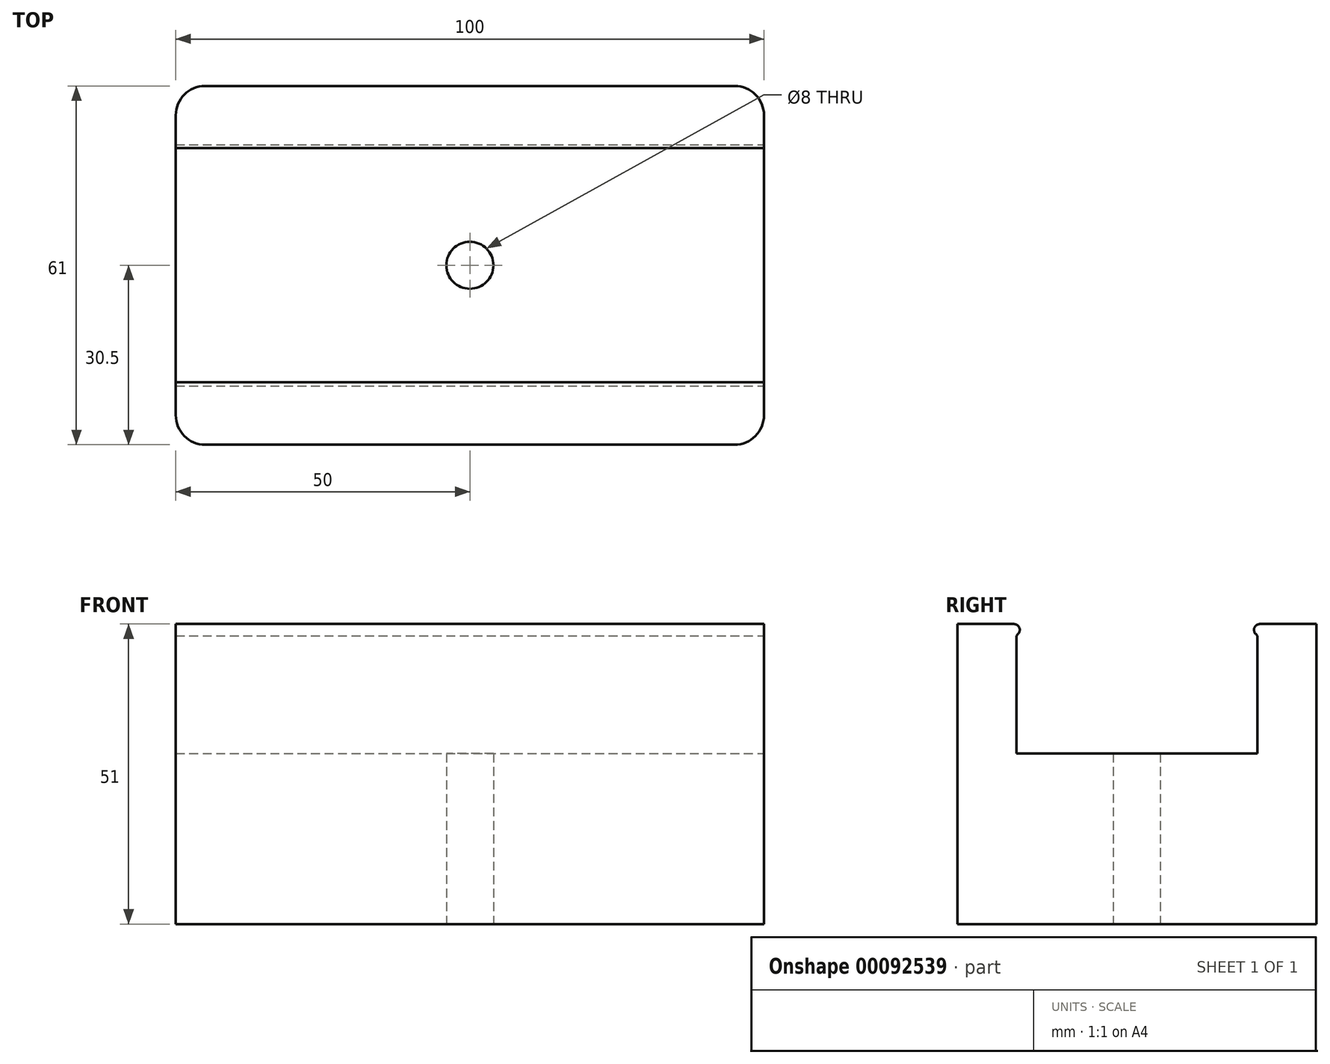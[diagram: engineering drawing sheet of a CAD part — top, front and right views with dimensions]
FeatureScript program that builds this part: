
annotation { "Feature Type Name" : "Feature", "Feature Type Description" : "" }
export const myFeature = defineFeature(function(context is Context, id is Id, definition is map)
    precondition{}
    {
        {
            var Q0;
            Q0=qCreatedBy(makeId("Top.planeOp"),FACE);
            var sketch = newSketch(context, id + "F0", { "sketchPlane" : qUnion([Q0])});
            skLineSegment(sketch, "E0.bottom", {"start": v(0, 0) * mm, "end": v(100, 0) * mm});
            skLineSegment(sketch, "E0.top", {"start": v(0, -61) * mm, "end": v(100, -61) * mm});
            skLineSegment(sketch, "E0.left", {"start": v(0, 0) * mm, "end": v(0, -61) * mm});
            skLineSegment(sketch, "E0.right", {"start": v(100, 0) * mm, "end": v(100, -61) * mm});
            skLineSegment(sketch, "E1", {"start": v(0, -30.5) * mm, "end": v(100, -30.5) * mm});
            skLineSegment(sketch, "E2", {"start": v(0, -51) * mm, "end": v(100, -51) * mm});
            skLineSegment(sketch, "E3", {"start": v(0, -10) * mm, "end": v(100, -10) * mm});
            skLineSegment(sketch, "E4", {"start": v(100, -10) * mm, "end": v(100, -30.5) * mm});
            skLineSegment(sketch, "E5", {"start": v(100, -51) * mm, "end": v(100, -30.5) * mm});
            skCircle(sketch, "E6", {"center": v(50, -30.5) * mm, "radius": 4 * mm});
            skCircle(sketch, "E7", {"center": v(50, -30.5) * mm, "radius": 1 * mm});
            skSolve(sketch);
        }
        {
            var Q0;
            {var subQ0=sQuery(id+"F0.wireOp",EDGE,"E0.bottom");Q0=makeQuery(id+"F0.imprint","IMPRINT",FACE,{"disambiguationData":[TD([[makeQuery(id+"F0.imprint","IMPRINT",EDGE,{"derivedFrom":subQ0}),-1.0]])]});}
            var Q1;
            {var subQ0=sQuery(id+"F0.wireOp",EDGE,"E0.top");Q1=makeQuery(id+"F0.imprint","IMPRINT",FACE,{"disambiguationData":[TD([[makeQuery(id+"F0.imprint","IMPRINT",EDGE,{"derivedFrom":subQ0}),1.0]])]});}
            extrude(context, id + "F1", {"entities" : qUnion([Q0, Q1]), "depth" : 51 * mm});
        }
        {
            var Q0;
            {var subQ0=sQuery(id+"F0.wireOp",EDGE,"E0.bottom");Q0=makeQuery(id+"F0.imprint","IMPRINT",FACE,{"disambiguationData":[TD([[makeQuery(id+"F0.imprint","IMPRINT",EDGE,{"derivedFrom":subQ0}),-1.0]])]});}
            var Q1;
            {var subQ0=sQuery(id+"F0.wireOp",EDGE,"E0.top");Q1=makeQuery(id+"F0.imprint","IMPRINT",FACE,{"disambiguationData":[TD([[makeQuery(id+"F0.imprint","IMPRINT",EDGE,{"derivedFrom":subQ0}),1.0]])]});}
            var Q2;
            {var subQ8=sQuery(id+"F0.wireOp",EDGE,"E3");Q2=makeQuery(id+"F0.imprint","IMPRINT",FACE,{"disambiguationData":[TD([[makeQuery(id+"F0.imprint","IMPRINT",EDGE,{"derivedFrom":subQ8}),-1.0]])]});}
            var Q3;
            {var subQ8=sQuery(id+"F0.wireOp",EDGE,"E2");Q3=makeQuery(id+"F0.imprint","IMPRINT",FACE,{"disambiguationData":[TD([[makeQuery(id+"F0.imprint","IMPRINT",EDGE,{"derivedFrom":subQ8}),1.0]])]});}
            extrude(context, id + "F2", {"entities" : qUnion([Q0, Q1, Q2, Q3]), "depth" : 26 * mm});
        }
        {
            var Q0;
            {var subQ0=sQuery(id+"F0.wireOp",EDGE,"E6");var subQ1=sQuery(id+"F0.wireOp",EDGE,"E1");var subQ2=makeQuery(id+"F0.imprint","INTERSECT",VERTEX,{"disambiguationData":[OD(0.0)],"derivedFrom":[subQ1,subQ0]});Q0=makeQuery(id+"F0.imprint","IMPRINT",FACE,{"disambiguationData":[TD([[makeQuery(id+"F0.imprint","IMPRINT",EDGE,{"disambiguationData":[TD([[subQ2,1.0]])],"derivedFrom":subQ1}),1.0]])]});}
            var Q1;
            {var subQ0=sQuery(id+"F0.wireOp",EDGE,"E6");var subQ1=sQuery(id+"F0.wireOp",EDGE,"E1");var subQ2=makeQuery(id+"F0.imprint","INTERSECT",VERTEX,{"disambiguationData":[OD(0.0)],"derivedFrom":[subQ1,subQ0]});Q1=makeQuery(id+"F0.imprint","IMPRINT",FACE,{"disambiguationData":[TD([[makeQuery(id+"F0.imprint","IMPRINT",EDGE,{"disambiguationData":[TD([[subQ2,1.0]])],"derivedFrom":subQ1}),-1.0]])]});}
            extrude(context, id + "F3", {"entities" : qUnion([Q0, Q1]), "operationType" : NewBodyOperationType.ADD, "depth" : 29 * mm});
        }
        {
            var Q0;
            Q0=makeQuery(id+"F1.opExtrude","SWEPT_EDGE",EDGE,{"disambiguationData":[OSD([sQuery(id+"F0.wireOp",EDGE,"E0.bottom"),sQuery(id+"F0.wireOp",EDGE,"E0.right")])]});
            var Q1;
            Q1=makeQuery(id+"F1.opExtrude","SWEPT_EDGE",EDGE,{"disambiguationData":[OSD([sQuery(id+"F0.wireOp",EDGE,"E0.bottom"),sQuery(id+"F0.wireOp",EDGE,"E0.left")])]});
            var Q2;
            Q2=makeQuery(id+"F1.opExtrude","SWEPT_EDGE",EDGE,{"disambiguationData":[OSD([sQuery(id+"F0.wireOp",EDGE,"E0.top"),sQuery(id+"F0.wireOp",EDGE,"E0.right")])]});
            var Q3;
            Q3=makeQuery(id+"F1.opExtrude","SWEPT_EDGE",EDGE,{"disambiguationData":[OSD([sQuery(id+"F0.wireOp",EDGE,"E0.top"),sQuery(id+"F0.wireOp",EDGE,"E0.left")])]});
            fillet(context, id + "F4", {"entities" : qUnion([Q0, Q1, Q2, Q3]), "radius" : 5 * mm, "tangentPropagation" : true, "allowEdgeOverflow" : false});
        }
        {
            var Q0;
            Q0=makeQuery(id+"F1.opExtrude","CAP_FACE",FACE,{"disambiguationData":[OSD([sQuery(id+"F0.wireOp",EDGE,"E0.bottom"),sQuery(id+"F0.wireOp",EDGE,"E0.left"),sQuery(id+"F0.wireOp",EDGE,"E0.right"),sQuery(id+"F0.wireOp",EDGE,"E3")])],"isStart":false});
            var sketch = newSketch(context, id + "F5", { "sketchPlane" : qUnion([Q0])});
            skLineSegment(sketch, "E8.bottom", {"start": v(0, -10) * mm, "end": v(100, -10) * mm});
            skLineSegment(sketch, "E8.top", {"start": v(0, -13) * mm, "end": v(100, -13) * mm});
            skLineSegment(sketch, "E8.left", {"start": v(0, -10) * mm, "end": v(0, -13) * mm});
            skLineSegment(sketch, "E8.right", {"start": v(100, -10) * mm, "end": v(100, -13) * mm});
            skSolve(sketch);
        }
        {
            var Q0;
            Q0=makeQuery(id+"F5.imprint","IMPRINT",FACE,{"disambiguationData":[TD([[makeQuery(id+"F5.imprint","IMPRINT",EDGE,{"derivedFrom":sQuery(id+"F5.wireOp",EDGE,"E8.bottom")}),-1.0]])]});
            extrude(context, id + "F6", {"entities" : qUnion([Q0]), "operationType" : NewBodyOperationType.ADD, "oppositeDirection" : true, "depth" : 2 * mm});
        }
        {
            var Q0;
            Q0=makeQuery(id+"F6.opExtrude","CAP_EDGE",EDGE,{"disambiguationData":[OSD([sQuery(id+"F5.wireOp",EDGE,"E8.top")])],"isStart":false});
            chamfer(context, id + "F7", {"entities" : qUnion([Q0]), "width" : 3 * mm, "tangentPropagation" : true});
        }
        {
            var Q0;
            Q0=makeQuery(id+"F1.opExtrude","CAP_FACE",FACE,{"disambiguationData":[OSD([sQuery(id+"F0.wireOp",EDGE,"E0.top"),sQuery(id+"F0.wireOp",EDGE,"E0.left"),sQuery(id+"F0.wireOp",EDGE,"E0.right"),sQuery(id+"F0.wireOp",EDGE,"E2")])],"isStart":false});
            var sketch = newSketch(context, id + "F8", { "sketchPlane" : qUnion([Q0])});
            skLineSegment(sketch, "E9.bottom", {"start": v(100, -51) * mm, "end": v(0, -51) * mm});
            skLineSegment(sketch, "E9.top", {"start": v(100, -48) * mm, "end": v(0, -48) * mm});
            skLineSegment(sketch, "E9.left", {"start": v(100, -51) * mm, "end": v(100, -48) * mm});
            skLineSegment(sketch, "E9.right", {"start": v(0, -51) * mm, "end": v(0, -48) * mm});
            skSolve(sketch);
        }
        {
            var Q0;
            Q0=makeQuery(id+"F8.imprint","IMPRINT",FACE,{"disambiguationData":[TD([[makeQuery(id+"F8.imprint","IMPRINT",EDGE,{"derivedFrom":sQuery(id+"F8.wireOp",EDGE,"E9.bottom")}),1.0]])]});
            extrude(context, id + "F9", {"entities" : qUnion([Q0]), "operationType" : NewBodyOperationType.ADD, "oppositeDirection" : true, "depth" : 2 * mm});
        }
        {
            var Q0;
            Q0=makeQuery(id+"F9.opExtrude","CAP_EDGE",EDGE,{"disambiguationData":[OSD([sQuery(id+"F8.wireOp",EDGE,"E9.top")])],"isStart":false});
            chamfer(context, id + "F10", {"entities" : qUnion([Q0]), "width" : 3 * mm, "tangentPropagation" : true});
        }
        {
            var Q0;
            {var subQ0=sQuery(id+"F5.wireOp",EDGE,"E8.top");Q0=makeQuery(id+"F7.opChamfer","BLEND_EDGE",EDGE,{"blendedFrom":[makeQuery(id+"F6.opExtrude","CAP_EDGE",EDGE,{"disambiguationData":[OSD([subQ0])],"isStart":false}),makeQuery(id+"F6.boolean.opBoolean","MERGE",FACE,{"derivedFrom":[makeQuery(id+"F1.opExtrude","CAP_FACE",FACE,{"disambiguationData":[OSD([sQuery(id+"F0.wireOp",EDGE,"E0.bottom"),sQuery(id+"F0.wireOp",EDGE,"E0.left"),sQuery(id+"F0.wireOp",EDGE,"E0.right"),sQuery(id+"F0.wireOp",EDGE,"E3")])],"isStart":false}),makeQuery(id+"F6.opExtrude","CAP_FACE",FACE,{"disambiguationData":[OSD([sQuery(id+"F5.wireOp",EDGE,"E8.bottom"),subQ0,sQuery(id+"F5.wireOp",EDGE,"E8.left"),sQuery(id+"F5.wireOp",EDGE,"E8.right")])],"isStart":true})]})],"blendedInto":[makeQuery(id+"F6.boolean.opBoolean","MERGE",FACE,{"derivedFrom":[makeQuery(id+"F1.opExtrude","CAP_FACE",FACE,{"disambiguationData":[OSD([sQuery(id+"F0.wireOp",EDGE,"E0.bottom"),sQuery(id+"F0.wireOp",EDGE,"E0.left"),sQuery(id+"F0.wireOp",EDGE,"E0.right"),sQuery(id+"F0.wireOp",EDGE,"E3")])],"isStart":false}),makeQuery(id+"F6.opExtrude","CAP_FACE",FACE,{"disambiguationData":[OSD([sQuery(id+"F5.wireOp",EDGE,"E8.bottom"),subQ0,sQuery(id+"F5.wireOp",EDGE,"E8.left"),sQuery(id+"F5.wireOp",EDGE,"E8.right")])],"isStart":true})]})]});}
            var Q1;
            {var subQ0=sQuery(id+"F8.wireOp",EDGE,"E9.top");Q1=makeQuery(id+"F10.opChamfer","BLEND_EDGE",EDGE,{"blendedFrom":[makeQuery(id+"F9.opExtrude","CAP_EDGE",EDGE,{"disambiguationData":[OSD([subQ0])],"isStart":false}),makeQuery(id+"F9.boolean.opBoolean","MERGE",FACE,{"derivedFrom":[makeQuery(id+"F1.opExtrude","CAP_FACE",FACE,{"disambiguationData":[OSD([sQuery(id+"F0.wireOp",EDGE,"E0.top"),sQuery(id+"F0.wireOp",EDGE,"E0.left"),sQuery(id+"F0.wireOp",EDGE,"E0.right"),sQuery(id+"F0.wireOp",EDGE,"E2")])],"isStart":false}),makeQuery(id+"F9.opExtrude","CAP_FACE",FACE,{"disambiguationData":[OSD([sQuery(id+"F8.wireOp",EDGE,"E9.bottom"),subQ0,sQuery(id+"F8.wireOp",EDGE,"E9.left"),sQuery(id+"F8.wireOp",EDGE,"E9.right")])],"isStart":true})]})],"blendedInto":[makeQuery(id+"F9.boolean.opBoolean","MERGE",FACE,{"derivedFrom":[makeQuery(id+"F1.opExtrude","CAP_FACE",FACE,{"disambiguationData":[OSD([sQuery(id+"F0.wireOp",EDGE,"E0.top"),sQuery(id+"F0.wireOp",EDGE,"E0.left"),sQuery(id+"F0.wireOp",EDGE,"E0.right"),sQuery(id+"F0.wireOp",EDGE,"E2")])],"isStart":false}),makeQuery(id+"F9.opExtrude","CAP_FACE",FACE,{"disambiguationData":[OSD([sQuery(id+"F8.wireOp",EDGE,"E9.bottom"),subQ0,sQuery(id+"F8.wireOp",EDGE,"E9.left"),sQuery(id+"F8.wireOp",EDGE,"E9.right")])],"isStart":true})]})]});}
            fillet(context, id + "F11", {"entities" : qUnion([Q0, Q1]), "radius" : 1 * mm, "tangentPropagation" : true, "allowEdgeOverflow" : false});
        }
    });
